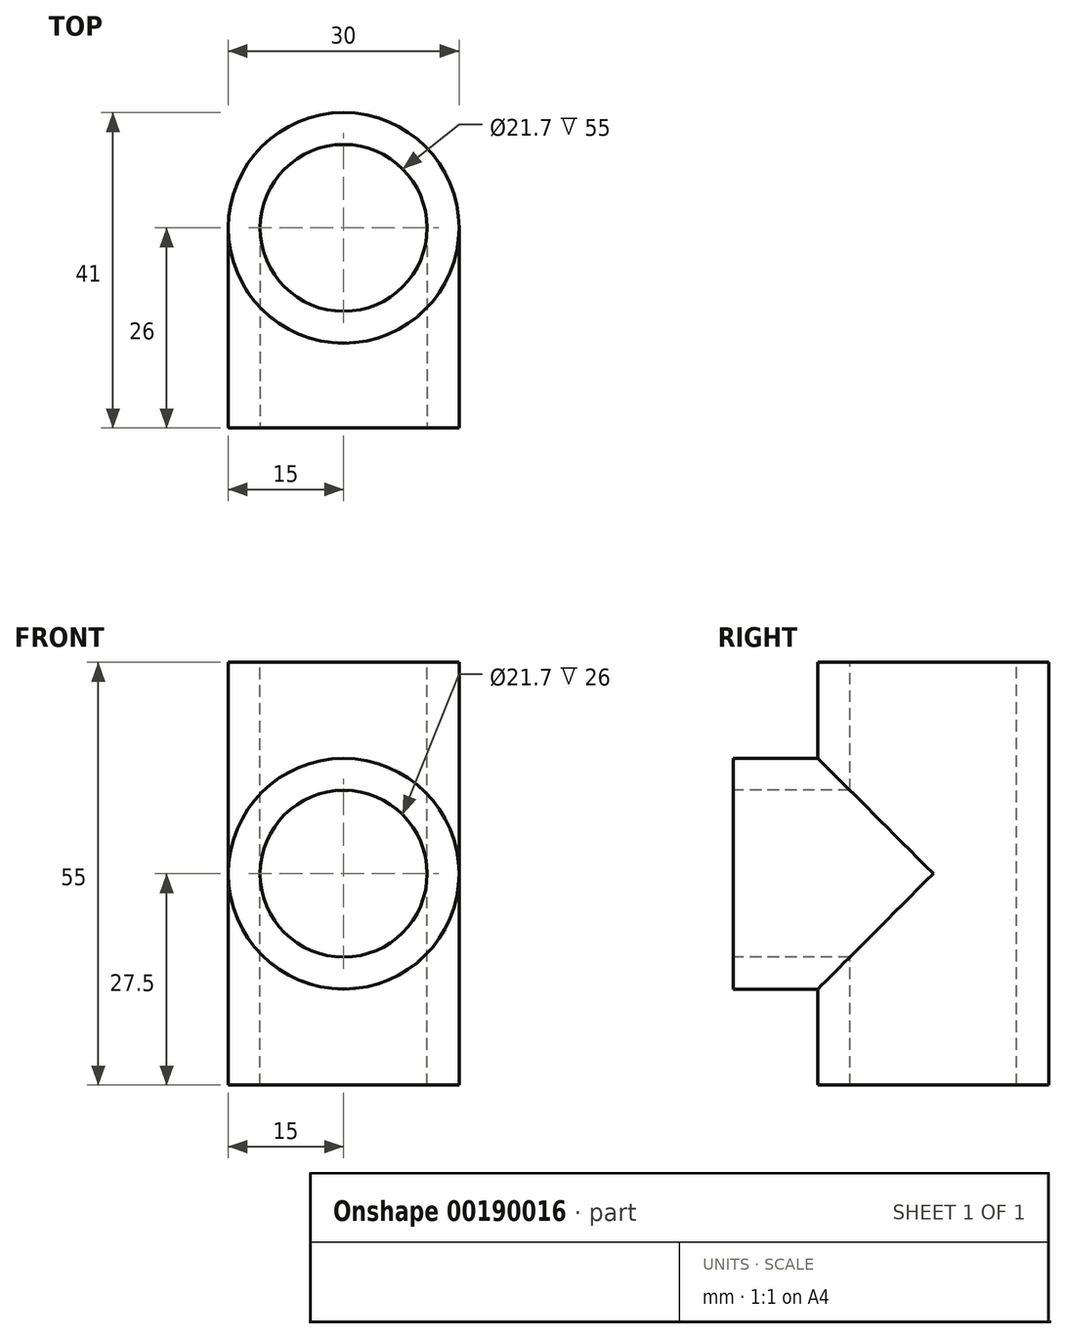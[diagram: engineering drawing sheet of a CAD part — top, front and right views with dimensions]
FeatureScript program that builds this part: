
annotation { "Feature Type Name" : "Feature", "Feature Type Description" : "" }
export const myFeature = defineFeature(function(context is Context, id is Id, definition is map)
    precondition{}
    {
        {
            var Q0;
            Q0=qCreatedBy(makeId("Top.planeOp"),FACE);
            var sketch = newSketch(context, id + "F0", { "sketchPlane" : qUnion([Q0])});
            skCircle(sketch, "E0", {"center": v(0, 0) * mm, "radius": 15 * mm});
            skSolve(sketch);
        }
        {
            var Q0;
            Q0 = qSketchRegion(id + "F0", true);
            extrude(context, id + "F1", {"entities" : qUnion([Q0]), "depth" : 55 * mm});
        }
        {
            var Q0;
            Q0=qCreatedBy(makeId("Front.planeOp"),FACE);
            var sketch = newSketch(context, id + "F2", { "sketchPlane" : qUnion([Q0])});
            skCircle(sketch, "E1", {"center": v(0, 27.5) * mm, "radius": 15 * mm});
            skSolve(sketch);
        }
        {
            var Q0;
            Q0 = qSketchRegion(id + "F2", true);
            extrude(context, id + "F3", {"entities" : qUnion([Q0]), "operationType" : NewBodyOperationType.ADD, "depth" : 26 * mm});
        }
        {
            var Q0;
            Q0=makeQuery(id+"F1.opExtrude","CAP_FACE",FACE,{"disambiguationData":[OSD([sQuery(id+"F0.wireOp",EDGE,"E0")])],"isStart":false});
            var sketch = newSketch(context, id + "F4", { "sketchPlane" : qUnion([Q0])});
            skCircle(sketch, "E2", {"center": v(0, 0) * mm, "radius": 10.85 * mm});
            skSolve(sketch);
        }
        {
            var Q0;
            Q0=makeQuery(id+"F4.imprint","IMPRINT",FACE,{"disambiguationData":[TD([[makeQuery(id+"F4.imprint","IMPRINT",EDGE,{"derivedFrom":sQuery(id+"F4.wireOp",EDGE,"E2")}),1.0]])]});
            extrude(context, id + "F5", {"entities" : qUnion([Q0]), "operationType" : NewBodyOperationType.REMOVE, "oppositeDirection" : true, "depth" : 55 * mm});
        }
        {
            var Q0;
            Q0=makeQuery(id+"F3.opExtrude","CAP_FACE",FACE,{"disambiguationData":[OSD([sQuery(id+"F2.wireOp",EDGE,"E1")])],"isStart":false});
            var sketch = newSketch(context, id + "F6", { "sketchPlane" : qUnion([Q0])});
            skCircle(sketch, "E3", {"center": v(0, 27.5) * mm, "radius": 10.85 * mm});
            skSolve(sketch);
        }
        {
            var Q0;
            Q0=makeQuery(id+"F6.imprint","IMPRINT",FACE,{"disambiguationData":[TD([[makeQuery(id+"F6.imprint","IMPRINT",EDGE,{"derivedFrom":sQuery(id+"F6.wireOp",EDGE,"E3")}),1.0]])]});
            extrude(context, id + "F7", {"entities" : qUnion([Q0]), "operationType" : NewBodyOperationType.REMOVE, "oppositeDirection" : true, "depth" : 26 * mm});
        }
    });
